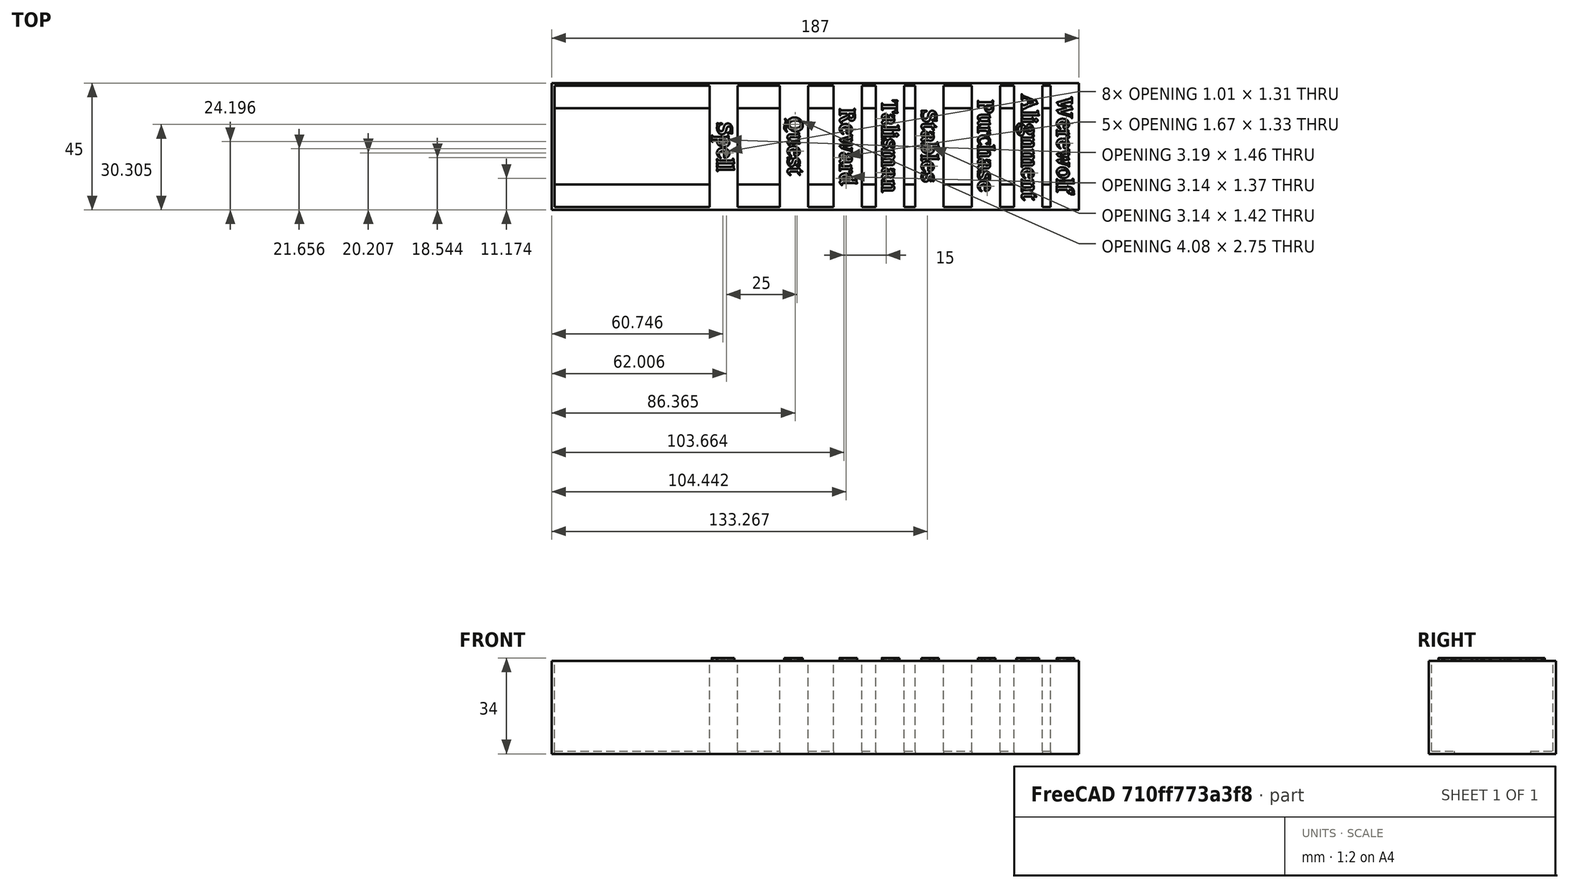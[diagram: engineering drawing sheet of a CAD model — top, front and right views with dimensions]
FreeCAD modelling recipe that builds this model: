
FCSTD DOCUMENT  (FreeCAD 0.18R4 (GitTag))
Label: common
License: All rights reserved
LicenseURL: http://en.wikipedia.org/wiki/All_rights_reserved
objects: Part::Box×14, Part::Part2DObjectPython×8, Part::Extrusion×8, Part::MultiFuse×4, Part::Cut×2
note: 36 computed .brp shape members not serialized (recipe doc carries the construction recipe); baked Part::Feature solids carry a one-line shape summary decoded from their .brp

FEATURE [Part::Box] Box  label="Cube"
  AttacherType = Attacher::AttachEngine3D
  Height = 33
  Length = 202
  Placement = pos=(0,-1,0) rot=(0,0,1;0rad)
  Width = 45
FEATURE [Part::Box] Box001  label="Cube001"
  AttacherType = Attacher::AttachEngine3D
  Height = 33
  Length = 200
  Placement = pos=(1,0,0) rot=(0,0,1;0rad)
  Width = 43
FEATURE [Part::Cut] Cut
  Base = -> Box
  Tool = -> Box001
FEATURE [Part::Box] Box002  label="Cube002"
  AttacherType = Attacher::AttachEngine3D
  Height = 1
  Length = 202
  Width = 8
FEATURE [Part::Box] Box003  label="Cube003"
  AttacherType = Attacher::AttachEngine3D
  Height = 1
  Length = 202
  Placement = pos=(0,35,0) rot=(0,0,1;0rad)
  Width = 8
FEATURE [Part::MultiFuse] Fusion
  Shapes = -> [Cut,Box002,Box003]
FEATURE [Part::Box] Box004  label="Cube004"
  AttacherType = Attacher::AttachEngine3D
  Height = 33
  Length = 10
  Placement = pos=(56,0,0) rot=(0,0,1;0rad)
  Width = 43
FEATURE [Part::Box] Box005  label="Cube005"
  AttacherType = Attacher::AttachEngine3D
  Height = 33
  Length = 10
  Placement = pos=(81,0,0) rot=(0,0,1;0rad)
  Width = 43
FEATURE [Part::Box] Box006  label="Cube006"
  AttacherType = Attacher::AttachEngine3D
  Height = 33
  Length = 10
  Placement = pos=(100,0,0) rot=(0,0,1;0rad)
  Width = 43
FEATURE [Part::Box] Box007  label="Cube007"
  AttacherType = Attacher::AttachEngine3D
  Height = 33
  Length = 10
  Placement = pos=(115,0,0) rot=(0,0,1;0rad)
  Width = 43
FEATURE [Part::Box] Box008  label="Cube008"
  AttacherType = Attacher::AttachEngine3D
  Height = 33
  Length = 10
  Placement = pos=(129,0,0) rot=(0,0,1;0rad)
  Width = 43
FEATURE [Part::Box] Box009  label="Cube009"
  AttacherType = Attacher::AttachEngine3D
  Height = 33
  Length = 10
  Placement = pos=(149,0,0) rot=(0,0,1;0rad)
  Width = 43
FEATURE [Part::Box] Box010  label="Cube010"
  AttacherType = Attacher::AttachEngine3D
  Height = 33
  Length = 10
  Placement = pos=(164,0,0) rot=(0,0,1;0rad)
  Width = 43
FEATURE [Part::Box] Box011  label="Cube011"
  AttacherType = Attacher::AttachEngine3D
  Height = 33
  Length = 10
  Placement = pos=(177,-1,0) rot=(0,0,1;0rad)
  Width = 45
FEATURE [Part::Box] Box012  label="Cube012"
  AttacherType = Attacher::AttachEngine3D
  Height = 33
  Length = 25
  Placement = pos=(177,-1,0) rot=(0,0,1;0rad)
  Width = 45
FEATURE [Part::Box] Box013  label="Cube013"
  AttacherType = Attacher::AttachEngine3D
  Height = 33
  Length = 10
  Placement = pos=(177,0,0) rot=(0,0,1;0rad)
  Width = 43
FEATURE [Part::Part2DObjectPython] ShapeString  # Draft 2D object (typed FeaturePython)
  FontFile = <userpath>/Downloads/talisman/Caxton Bold.otf
  Placement = pos=(60.28,21.01,33) rot=(0,0,-1;1.5708rad)
  Size = 3
  String = Spell
  Tracking = 0
FEATURE [Part::Part2DObjectPython] ShapeString001  # Draft 2D object (typed FeaturePython)
  FontFile = <userpath>/Downloads/talisman/Caxton Bold.otf
  Placement = pos=(57.28,40.01,33) rot=(0,0,-1;1.5708rad)
  Size = 3
  String = Quest
  Tracking = 0
FEATURE [Part::Part2DObjectPython] ShapeString002  # Draft 2D object (typed FeaturePython)
  FontFile = <userpath>/Downloads/talisman/Caxton Bold.otf
  Placement = pos=(60.28,21.01,33) rot=(0,0,-1;1.5708rad)
  Size = 3
  String = Reward
  Tracking = 0
FEATURE [Part::Part2DObjectPython] ShapeString003  # Draft 2D object (typed FeaturePython)
  FontFile = <userpath>/Downloads/talisman/Caxton Bold.otf
  Placement = pos=(60.28,21.01,33) rot=(0,0,-1;1.5708rad)
  Size = 3
  String = Talisman
  Tracking = 0
FEATURE [Part::Part2DObjectPython] ShapeString004  # Draft 2D object (typed FeaturePython)
  FontFile = <userpath>/Downloads/talisman/Caxton Bold.otf
  Placement = pos=(60.28,21.01,33) rot=(0,0,-1;1.5708rad)
  Size = 3
  String = Stables
  Tracking = 0
FEATURE [Part::Part2DObjectPython] ShapeString005  # Draft 2D object (typed FeaturePython)
  FontFile = <userpath>/Downloads/talisman/Caxton Bold.otf
  Placement = pos=(60.28,21.01,33) rot=(0,0,-1;1.5708rad)
  Size = 3
  String = Purchase
  Tracking = 0
FEATURE [Part::Part2DObjectPython] ShapeString006  # Draft 2D object (typed FeaturePython)
  FontFile = <userpath>/Downloads/talisman/Caxton Bold.otf
  Placement = pos=(60.28,21.01,33) rot=(0,0,-1;1.5708rad)
  Size = 3
  String = Alignment
  Tracking = 0
FEATURE [Part::MultiFuse] Fusion001
  Shapes = -> [Fusion,Box009,Box006,Box007,Box005,Box004,Box010,Box008,Box013]
FEATURE [Part::Cut] Cut001
  Base = -> Fusion001
  Tool = -> Box012
FEATURE [Part::MultiFuse] Fusion002
  Shapes = -> [Cut001,Box011]
FEATURE [Part::Part2DObjectPython] ShapeString007  # Draft 2D object (typed FeaturePython)
  FontFile = <userpath>/Downloads/talisman/Caxton Bold.otf
  Placement = pos=(60.28,21.01,33) rot=(0,0,-1;1.5708rad)
  Size = 3
  String = Werewolf 
  Tracking = 0
FEATURE [Part::Extrusion] Extrude
  Base = -> ShapeString
  Dir = (0,0,1)
  DirMode = 2
  FaceMakerClass = Part::FaceMakerBullseye
  LengthFwd = 1
  LengthRev = 0
  Placement = pos=(-1.5,9,0) rot=(0,0,1;0rad)
  Solid = false
  Symmetric = false
FEATURE [Part::Extrusion] Extrude001
  Base = -> ShapeString001
  Dir = (0,0,1)
  DirMode = 2
  FaceMakerClass = Part::FaceMakerBullseye
  LengthFwd = 1
  LengthRev = 0
  Placement = pos=(26.5,-8,0) rot=(0,0,1;0rad)
  Solid = false
  Symmetric = false
FEATURE [Part::Extrusion] Extrude002
  Base = -> ShapeString002
  Dir = (0,0,1)
  DirMode = 2
  FaceMakerClass = Part::FaceMakerBullseye
  LengthFwd = 1
  LengthRev = 0
  Placement = pos=(42,14,0) rot=(0,0,1;0rad)
  Solid = false
  Symmetric = false
FEATURE [Part::Extrusion] Extrude003
  Base = -> ShapeString003
  Dir = (0,0,1)
  DirMode = 2
  FaceMakerClass = Part::FaceMakerBullseye
  LengthFwd = 1
  LengthRev = 0
  Placement = pos=(57,17,0) rot=(0,0,1;0rad)
  Solid = false
  Symmetric = false
FEATURE [Part::Extrusion] Extrude004
  Base = -> ShapeString004
  Dir = (0,0,1)
  DirMode = 2
  FaceMakerClass = Part::FaceMakerBullseye
  LengthFwd = 1
  LengthRev = 0
  Placement = pos=(71,13.5,0) rot=(0,0,1;0rad)
  Solid = false
  Symmetric = false
FEATURE [Part::Extrusion] Extrude005
  Base = -> ShapeString005
  Dir = (0,0,1)
  DirMode = 2
  FaceMakerClass = Part::FaceMakerBullseye
  LengthFwd = 1
  LengthRev = 0
  Placement = pos=(91,17,0) rot=(0,0,1;0rad)
  Solid = false
  Symmetric = false
FEATURE [Part::Extrusion] Extrude006
  Base = -> ShapeString006
  Dir = (0,0,1)
  DirMode = 2
  FaceMakerClass = Part::FaceMakerBullseye
  LengthFwd = 1
  LengthRev = 0
  Placement = pos=(106.5,19,0) rot=(0,0,1;0rad)
  Solid = false
  Symmetric = false
FEATURE [Part::Extrusion] Extrude007
  Base = -> ShapeString007
  Dir = (0,0,1)
  DirMode = 2
  FaceMakerClass = Part::FaceMakerBullseye
  LengthFwd = 1
  LengthRev = 0
  Placement = pos=(119,18,0) rot=(0,0,1;0rad)
  Solid = false
  Symmetric = false
FEATURE [Part::MultiFuse] Fusion003
  Shapes = -> [Extrude003,Extrude,Extrude002,Extrude005,Extrude006,Extrude007,Extrude004,Extrude001]
